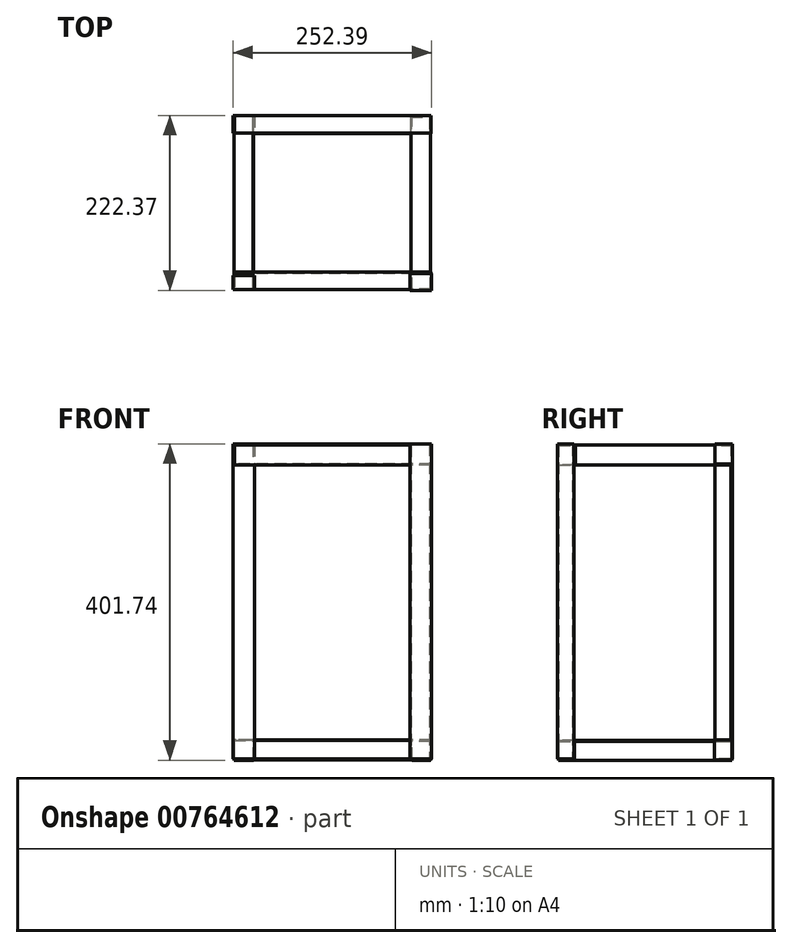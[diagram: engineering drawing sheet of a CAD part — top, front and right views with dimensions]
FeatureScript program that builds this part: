
annotation { "Feature Type Name" : "Feature", "Feature Type Description" : "" }
export const myFeature = defineFeature(function(context is Context, id is Id, definition is map)
    precondition{}
    {
        {
            var Q0;
            Q0=qCreatedBy(makeId("Front.planeOp"),FACE);
            var sketch = newSketch(context, id + "F0", { "sketchPlane" : qUnion([Q0])});
            skLineSegment(sketch, "E0.bottom", {"start": v(124.32, 248.55) * mm, "end": v(-125.68, 248.55) * mm});
            skLineSegment(sketch, "E0.top", {"start": v(124.32, -151.45) * mm, "end": v(-125.68, -151.45) * mm});
            skLineSegment(sketch, "E0.left", {"start": v(124.32, 248.55) * mm, "end": v(124.32, -151.45) * mm});
            skLineSegment(sketch, "E0.right", {"start": v(-125.68, 248.55) * mm, "end": v(-125.68, -151.45) * mm});
            skSolve(sketch);
        }
        {
            var Q0;
            Q0=makeQuery(id+"F0.imprint","IMPRINT",FACE,{"disambiguationData":[TD([[makeQuery(id+"F0.imprint","IMPRINT",EDGE,{"derivedFrom":sQuery(id+"F0.wireOp",EDGE,"E0.bottom")}),1.0]])]});
            var sketch = newSketch(context, id + "F1", { "sketchPlane" : qUnion([Q0])});
            skLineSegment(sketch, "E1.bottom", {"start": v(124.32, 248.9) * mm, "end": v(99.32, 248.9) * mm});
            skLineSegment(sketch, "E1.top", {"start": v(124.32, 223.34) * mm, "end": v(99.32, 223.34) * mm});
            skLineSegment(sketch, "E1.left", {"start": v(124.32, 248.9) * mm, "end": v(124.32, 223.34) * mm});
            skLineSegment(sketch, "E1.right", {"start": v(99.32, 248.9) * mm, "end": v(99.32, 223.34) * mm});
            skLineSegment(sketch, "E2.bottom", {"start": v(-125.68, 248.55) * mm, "end": v(-101.64, 248.55) * mm});
            skLineSegment(sketch, "E2.top", {"start": v(-125.68, 223.34) * mm, "end": v(-101.64, 223.34) * mm});
            skLineSegment(sketch, "E2.left", {"start": v(-125.68, 248.55) * mm, "end": v(-125.68, 223.34) * mm});
            skLineSegment(sketch, "E2.right", {"start": v(-101.64, 248.55) * mm, "end": v(-101.64, 223.34) * mm});
            skLineSegment(sketch, "E3.bottom", {"start": v(124.32, -151.45) * mm, "end": v(100.86, -151.45) * mm});
            skLineSegment(sketch, "E3.top", {"start": v(124.32, -127.44) * mm, "end": v(100.86, -127.44) * mm});
            skLineSegment(sketch, "E3.left", {"start": v(124.32, -151.45) * mm, "end": v(124.32, -127.44) * mm});
            skLineSegment(sketch, "E3.right", {"start": v(100.86, -151.45) * mm, "end": v(100.86, -127.44) * mm});
            skLineSegment(sketch, "E4.bottom", {"start": v(-125.68, -151.45) * mm, "end": v(-100.68, -151.45) * mm});
            skLineSegment(sketch, "E4.top", {"start": v(-125.68, -126.45) * mm, "end": v(-100.68, -126.45) * mm});
            skLineSegment(sketch, "E4.left", {"start": v(-125.68, -151.45) * mm, "end": v(-125.68, -126.45) * mm});
            skLineSegment(sketch, "E4.right", {"start": v(-100.68, -151.45) * mm, "end": v(-100.68, -126.45) * mm});
            skSolve(sketch);
        }
        {
            var Q0;
            Q0 = qSketchRegion(id + "F1", true);
            extrude(context, id + "F2", {"entities" : qUnion([Q0]), "depth" : 110 * mm, "offsetDistance" : 25 * mm, "hasSecondDirection" : true, "secondDirectionOppositeDirection" : true, "secondDirectionDepth" : 110 * mm});
        }
        {
            var Q0;
            Q0=qCreatedBy(makeId("Top.planeOp"),FACE);
            var sketch = newSketch(context, id + "F3", { "sketchPlane" : qUnion([Q0])});
            skLineSegment(sketch, "E5.bottom", {"start": v(-99.74, 110.58) * mm, "end": v(-126.97, 110.58) * mm});
            skLineSegment(sketch, "E5.top", {"start": v(-99.74, 88.56) * mm, "end": v(-126.97, 88.56) * mm});
            skLineSegment(sketch, "E5.left", {"start": v(-99.74, 110.58) * mm, "end": v(-99.74, 88.56) * mm});
            skLineSegment(sketch, "E5.right", {"start": v(-126.97, 110.58) * mm, "end": v(-126.97, 88.56) * mm});
            skLineSegment(sketch, "E6.bottom", {"start": v(-126.97, -92.22) * mm, "end": v(-99.74, -92.22) * mm});
            skLineSegment(sketch, "E6.top", {"start": v(-126.97, -110.27) * mm, "end": v(-99.74, -110.27) * mm});
            skLineSegment(sketch, "E6.left", {"start": v(-126.97, -92.22) * mm, "end": v(-126.97, -110.27) * mm});
            skLineSegment(sketch, "E6.right", {"start": v(-99.74, -92.22) * mm, "end": v(-99.74, -110.27) * mm});
            skLineSegment(sketch, "E7.bottom", {"start": v(98.99, 108.83) * mm, "end": v(122.88, 108.83) * mm});
            skLineSegment(sketch, "E7.top", {"start": v(98.99, 88.56) * mm, "end": v(122.88, 88.56) * mm});
            skLineSegment(sketch, "E7.left", {"start": v(98.99, 108.83) * mm, "end": v(98.99, 88.56) * mm});
            skLineSegment(sketch, "E7.right", {"start": v(122.88, 108.83) * mm, "end": v(122.88, 88.56) * mm});
            skLineSegment(sketch, "E8.bottom", {"start": v(125.42, -90.14) * mm, "end": v(98.28, -90.14) * mm});
            skLineSegment(sketch, "E8.top", {"start": v(125.42, -111.3) * mm, "end": v(98.28, -111.3) * mm});
            skLineSegment(sketch, "E8.left", {"start": v(125.42, -90.14) * mm, "end": v(125.42, -111.3) * mm});
            skLineSegment(sketch, "E8.right", {"start": v(98.28, -90.14) * mm, "end": v(98.28, -111.3) * mm});
            skSolve(sketch);
        }
        {
            var Q0;
            Q0=makeQuery(id+"F3.imprint","IMPRINT",FACE,{"disambiguationData":[TD([[makeQuery(id+"F3.imprint","IMPRINT",EDGE,{"derivedFrom":sQuery(id+"F3.wireOp",EDGE,"E5.bottom")}),1.0]])]});
            var Q1;
            Q1=makeQuery(id+"F3.imprint","IMPRINT",FACE,{"disambiguationData":[TD([[makeQuery(id+"F3.imprint","IMPRINT",EDGE,{"derivedFrom":sQuery(id+"F3.wireOp",EDGE,"E7.bottom")}),-1.0]])]});
            var Q2;
            Q2=makeQuery(id+"F3.imprint","IMPRINT",FACE,{"disambiguationData":[TD([[makeQuery(id+"F3.imprint","IMPRINT",EDGE,{"derivedFrom":sQuery(id+"F3.wireOp",EDGE,"E8.bottom")}),1.0]])]});
            var Q3;
            Q3=makeQuery(id+"F3.imprint","IMPRINT",FACE,{"disambiguationData":[TD([[makeQuery(id+"F3.imprint","IMPRINT",EDGE,{"derivedFrom":sQuery(id+"F3.wireOp",EDGE,"E6.bottom")}),-1.0]])]});
            extrude(context, id + "F4", {"entities" : qUnion([Q0, Q1, Q2, Q3]), "depth" : 250 * mm, "offsetDistance" : 25 * mm, "hasSecondDirection" : true, "secondDirectionOppositeDirection" : true, "secondDirectionDepth" : 150 * mm});
        }
        {
            var Q0;
            Q0=qCreatedBy(makeId("Right.planeOp"),FACE);
            var sketch = newSketch(context, id + "F5", { "sketchPlane" : qUnion([Q0])});
            skLineSegment(sketch, "E9.bottom", {"start": v(110.38, -151.37) * mm, "end": v(87.88, -151.37) * mm});
            skLineSegment(sketch, "E9.top", {"start": v(110.38, -125.43) * mm, "end": v(87.88, -125.43) * mm});
            skLineSegment(sketch, "E9.left", {"start": v(110.38, -151.37) * mm, "end": v(110.38, -125.43) * mm});
            skLineSegment(sketch, "E9.right", {"start": v(87.88, -151.37) * mm, "end": v(87.88, -125.43) * mm});
            skLineSegment(sketch, "E10.bottom", {"start": v(111.06, 224.9) * mm, "end": v(88.5, 224.9) * mm});
            skLineSegment(sketch, "E10.top", {"start": v(111.06, 250.3) * mm, "end": v(88.5, 250.3) * mm});
            skLineSegment(sketch, "E10.left", {"start": v(111.06, 224.9) * mm, "end": v(111.06, 250.3) * mm});
            skLineSegment(sketch, "E10.right", {"start": v(88.5, 224.9) * mm, "end": v(88.5, 250.3) * mm});
            skLineSegment(sketch, "E11.bottom", {"start": v(-89.8, -149.62) * mm, "end": v(-109.83, -149.62) * mm});
            skLineSegment(sketch, "E11.top", {"start": v(-89.8, -126.2) * mm, "end": v(-109.83, -126.2) * mm});
            skLineSegment(sketch, "E11.left", {"start": v(-89.8, -149.62) * mm, "end": v(-89.8, -126.2) * mm});
            skLineSegment(sketch, "E11.right", {"start": v(-109.83, -149.62) * mm, "end": v(-109.83, -126.2) * mm});
            skLineSegment(sketch, "E12.bottom", {"start": v(-88.26, 223.5) * mm, "end": v(-110.3, 223.5) * mm});
            skLineSegment(sketch, "E12.top", {"start": v(-88.26, 249.14) * mm, "end": v(-110.3, 249.14) * mm});
            skLineSegment(sketch, "E12.left", {"start": v(-88.26, 223.5) * mm, "end": v(-88.26, 249.14) * mm});
            skLineSegment(sketch, "E12.right", {"start": v(-110.3, 223.5) * mm, "end": v(-110.3, 249.14) * mm});
            skSolve(sketch);
        }
        {
            var Q0;
            Q0 = qSketchRegion(id + "F5", true);
            extrude(context, id + "F6", {"entities" : qUnion([Q0]), "depth" : 125 * mm, "offsetDistance" : 25 * mm, "hasSecondDirection" : true, "secondDirectionOppositeDirection" : true, "secondDirectionDepth" : 125 * mm});
        }
    });
